FCSTD DOCUMENT  (FreeCAD 0.18R4 (GitTag))
Label: SpeechLampMaia
License: All rights reserved
LicenseURL: http://en.wikipedia.org/wiki/All_rights_reserved
objects: Sketcher::SketchObject×1, PartDesign::Body×1
note: 2 computed .brp shape members not serialized (recipe doc carries the construction recipe); baked Part::Feature solids carry a one-line shape summary decoded from their .brp

FEATURE [Sketcher::SketchObject] Sketch
  MapMode = 5
  Support = -> [XY_Plane]
  sketch-geometry (5):
    g0: Ellipse CenterX=0 CenterY=0 CenterZ=0 NormalX=0 NormalY=0 NormalZ=1 MajorRadius=95 MinorRadius=70 AngleXU=0
    g1: LineSegment [constr] StartX=95 StartY=0 StartZ=0 EndX=-95 EndY=0 EndZ=0
    g2: LineSegment [constr] StartX=0 StartY=70 StartZ=0 EndX=0 EndY=-70 EndZ=0
    g3: LineSegment StartX=-35 StartY=-65.0761 StartZ=0 EndX=-90 EndY=-72 EndZ=0
    g4: LineSegment StartX=-90 StartY=-72 StartZ=0 EndX=-68 EndY=-48.8821 EndZ=0
  constraints (13):
    c: InternalAlignment(g1,g0)
    c: InternalAlignment(g2,g0)
    c: Coincident(g0,g-1)
    c: PointOnObject(g3,g0)
    c: Coincident(g4,g3)
    c: PointOnObject(g4,g0)
    c: DistanceY(g2,g2) = 140
    c: DistanceX(g1,g1) = 190
    c: DistanceX(g1,g4) = 27
    c: DistanceX(g1,g3) = 60
    c: DistanceY(g3,g1) = 72
    c: DistanceX(g3,g2) = 90
    c: Vertical(g2)
FEATURE [PartDesign::Body] Body
  Group = -> [Sketch]
  Origin = -> Origin
